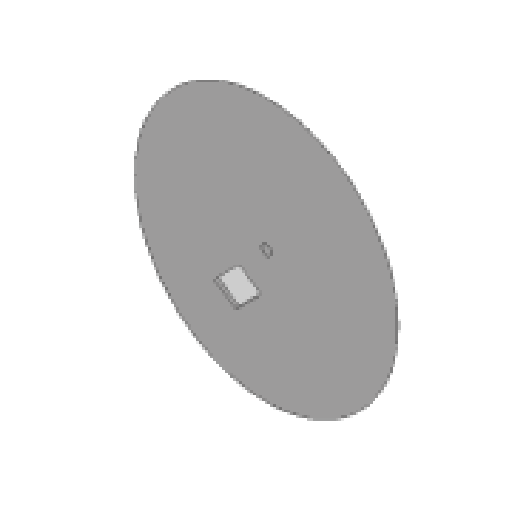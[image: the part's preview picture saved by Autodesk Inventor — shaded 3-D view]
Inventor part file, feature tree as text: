
AUTODESK INVENTOR PART (.ipt)
format: ipt  version: 2023 (Build 270158000, 158)  size: 109,056 bytes
history: native  units: in
note: dims shown in document units (in); Inventor stores cm internally (conversion verified against a paired STEP export)
features: extrude x4, sketch x4, projected_geometry x3
ambient origin geometry x8: Origin, YZ Plane, XZ Plane, XY Plane, X Axis, Y Axis, Z Axis, Center Point
bodies: Solid1 (feature_tree)
feature tree (11):
  extrude  "Extrusion1"  Depth=1.0in
  extrude  "Extrusion2"  Depth=78.7402in TaperAngle=0.0deg
  extrude  "Extrusion3"  Depth=1.0in
  extrude  "Extrusion4"  [1 undecoded]
  sketch  "Sketch1"  dims[d0=1.0in d1=0.0in d2=39.3701in]
  sketch  "Sketch2"  dims[d3=0.01in d4=0.0in d5=78.7402in d6=0.0in]
  projected_geometry  "Projected Loop1"
  sketch  "Sketch3"  dims[d7=1.0in d8=984.252in]
  projected_geometry  "Projected Loop2"
  sketch  "Sketch4"  dims[d9=7.874in d10=0.0in]
  projected_geometry  "Projected Loop3"
note: 1 required parameter value undecoded (feature->parameter linkage not recoverable at this tier; creation-order binding heuristic only, values carry confidence <= 0.55)
